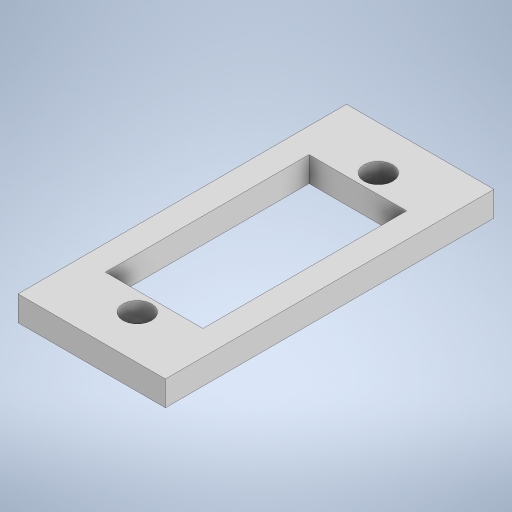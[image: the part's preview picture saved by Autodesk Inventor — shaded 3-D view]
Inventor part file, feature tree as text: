
AUTODESK INVENTOR PART (.ipt)
format: ipt  version: 2024.2 (Build 282272000, 272)  size: 238,592 bytes
history: native  units: mm
features: extrude x1, sketch x1
ambient origin geometry x8: Origin, YZ Plane, XZ Plane, XY Plane, X Axis, Y Axis, Z Axis, Center Point
bodies: Solid1 (feature_tree)
feature tree (2):
  extrude  "Extrusion1"  Depth=16.3mm
  sketch  "Sketch1"  dims[d0=7.8mm d1=16.3mm d2=2.0mm d3=2.0mm d4=5.0mm d5=5.0mm d6=2.3mm d7=2.3mm d8=1.5mm d9=1.5mm d10=3.75mm d11=2.0mm d12=0.0mm]
